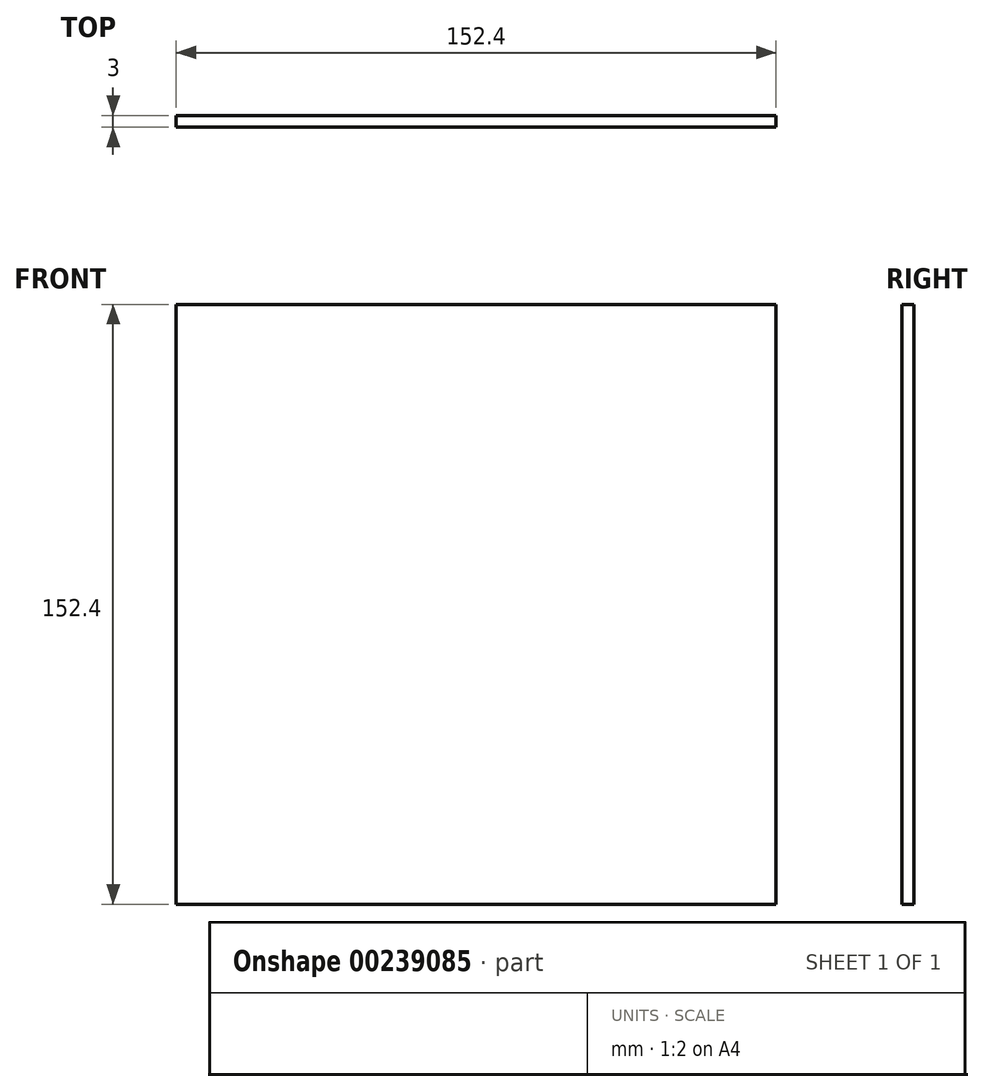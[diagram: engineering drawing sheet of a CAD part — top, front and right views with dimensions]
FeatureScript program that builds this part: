
annotation { "Feature Type Name" : "Feature", "Feature Type Description" : "" }
export const myFeature = defineFeature(function(context is Context, id is Id, definition is map)
    precondition{}
    {
        {
            assignVariable(context, id + "F0", {"name" : "v", "anyValue" : 3});
        }
        {
            var Q0;
            Q0=qCreatedBy(makeId("Front.planeOp"),FACE);
            var sketch = newSketch(context, id + "F1", { "sketchPlane" : qUnion([Q0])});
            skLineSegment(sketch, "E0.bottom", {"start": v(-76.2, 76.2) * mm, "end": v(76.2, 76.2) * mm});
            skLineSegment(sketch, "E0.top", {"start": v(-76.2, -76.2) * mm, "end": v(76.2, -76.2) * mm});
            skLineSegment(sketch, "E0.left", {"start": v(-76.2, 76.2) * mm, "end": v(-76.2, -76.2) * mm});
            skLineSegment(sketch, "E0.right", {"start": v(76.2, 76.2) * mm, "end": v(76.2, -76.2) * mm});
            skPoint(sketch, "E0.middle", {"position": v(0, 0) * mm});
            skSolve(sketch);
        }
        {
            var Q0;
            Q0 = qSketchRegion(id + "F1", true);
            extrude(context, id + "F2", {"entities" : qUnion([Q0]), "depth" : (getVariable(context, 'v')) * mm});
        }
    });
